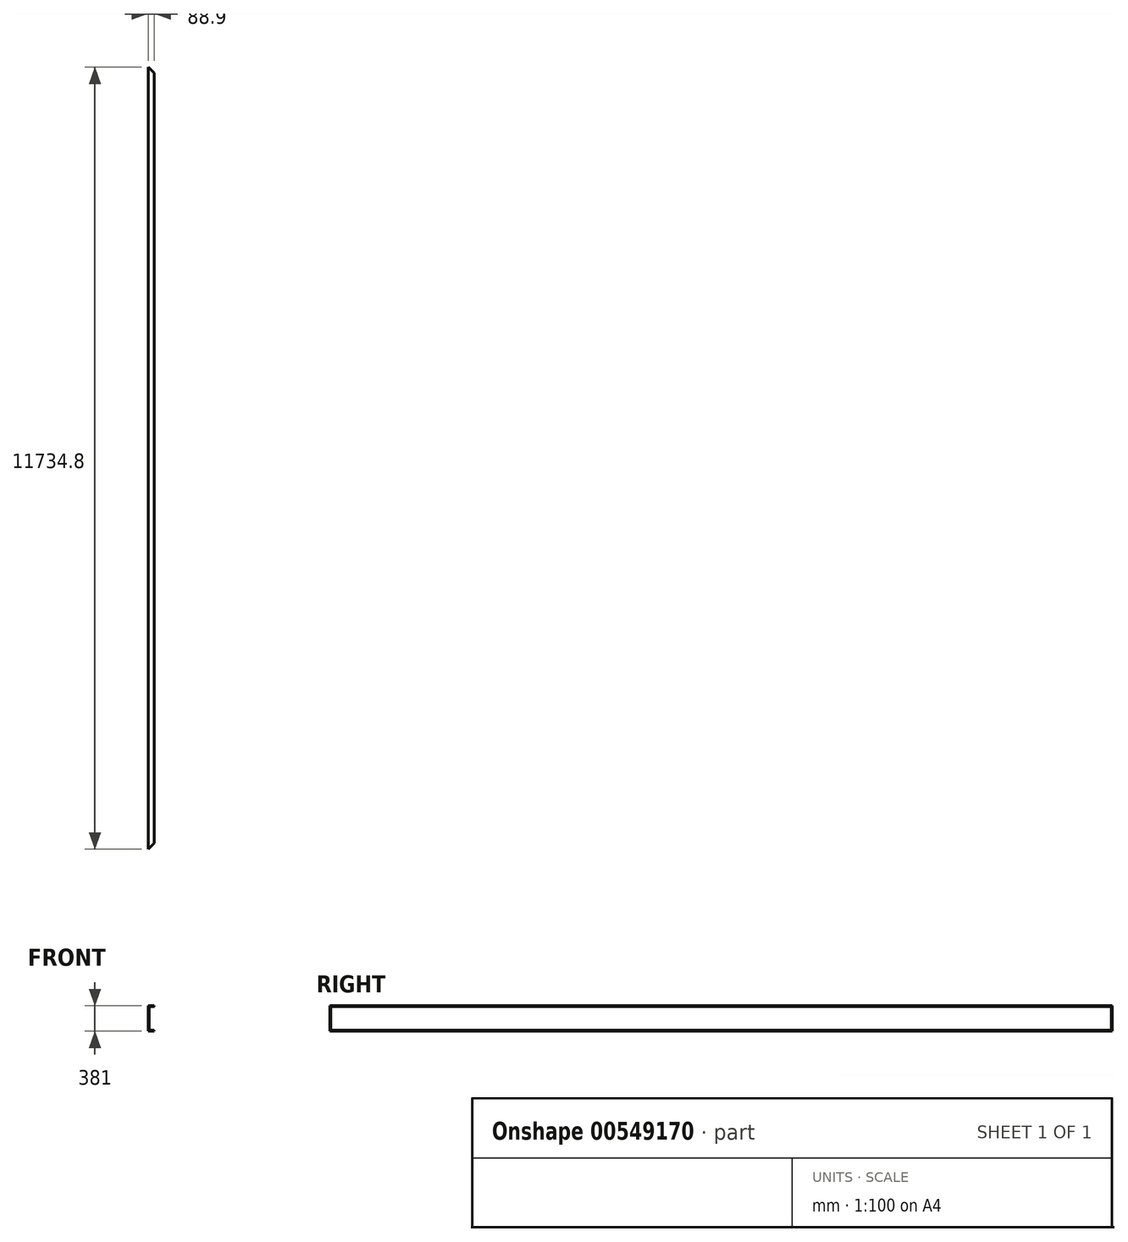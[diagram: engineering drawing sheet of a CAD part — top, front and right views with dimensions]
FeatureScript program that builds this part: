
annotation { "Feature Type Name" : "Feature", "Feature Type Description" : "" }
export const myFeature = defineFeature(function(context is Context, id is Id, definition is map)
    precondition{}
    {
        {
            var Q0;
            Q0=qCreatedBy(makeId("Front.planeOp"),FACE);
            var sketch = newSketch(context, id + "F0", { "sketchPlane" : qUnion([Q0])});
            skLineSegment(sketch, "E0", {"start": v(44.45, 190.5) * mm, "end": v(-44.45, 190.5) * mm});
            skLineSegment(sketch, "E1", {"start": v(-44.45, 190.5) * mm, "end": v(-44.45, -190.5) * mm});
            skLineSegment(sketch, "E2", {"start": v(-44.45, -190.5) * mm, "end": v(44.45, -190.5) * mm});
            skLineSegment(sketch, "E3", {"start": v(44.45, -190.5) * mm, "end": v(44.45, -177.8) * mm});
            skLineSegment(sketch, "E4", {"start": v(44.45, -177.8) * mm, "end": v(-31.75, -177.8) * mm});
            skLineSegment(sketch, "E5", {"start": v(-31.75, -177.8) * mm, "end": v(-31.75, 177.8) * mm});
            skLineSegment(sketch, "E6", {"start": v(-31.75, 177.8) * mm, "end": v(44.45, 177.8) * mm});
            skLineSegment(sketch, "E7", {"start": v(44.45, 177.8) * mm, "end": v(44.45, 190.5) * mm});
            skSolve(sketch);
        }
        {
            var Q0;
            Q0=makeQuery(id+"F0.imprint","IMPRINT",FACE,{"disambiguationData":[TD([[makeQuery(id+"F0.imprint","IMPRINT",EDGE,{"derivedFrom":sQuery(id+"F0.wireOp",EDGE,"E0")}),1.0]])]});
            extrude(context, id + "F1", {"entities" : qUnion([Q0]), "depth" : 11734.8 * mm});
        }
        {
            var Q0;
            Q0=makeQuery(id+"F1.opExtrude","SWEPT_EDGE",EDGE,{"disambiguationData":[OSD([sQuery(id+"F0.wireOp",EDGE,"E3"),sQuery(id+"F0.wireOp",EDGE,"E4")])]});
            var Q1;
            Q1=makeQuery(id+"F1.opExtrude","SWEPT_EDGE",EDGE,{"disambiguationData":[OSD([sQuery(id+"F0.wireOp",EDGE,"E4"),sQuery(id+"F0.wireOp",EDGE,"E5")])]});
            var Q2;
            Q2=makeQuery(id+"F1.opExtrude","SWEPT_EDGE",EDGE,{"disambiguationData":[OSD([sQuery(id+"F0.wireOp",EDGE,"E5"),sQuery(id+"F0.wireOp",EDGE,"E6")])]});
            var Q3;
            Q3=makeQuery(id+"F1.opExtrude","SWEPT_EDGE",EDGE,{"disambiguationData":[OSD([sQuery(id+"F0.wireOp",EDGE,"E6"),sQuery(id+"F0.wireOp",EDGE,"E7")])]});
            fillet(context, id + "F2", {"entities" : qUnion([Q0, Q1, Q2, Q3]), "radius" : 7.62 * mm, "tangentPropagation" : true, "allowEdgeOverflow" : false});
        }
        {
            var Q0;
            Q0=makeQuery(id+"F1.opExtrude","SWEPT_FACE",FACE,{"disambiguationData":[OSD([sQuery(id+"F0.wireOp",EDGE,"E0")])]});
            var sketch = newSketch(context, id + "F3", { "sketchPlane" : qUnion([Q0])});
            skLineSegment(sketch, "E8", {"start": v(-44.45, 0) * mm, "end": v(44.45, -88.9) * mm});
            skLineSegment(sketch, "E9", {"start": v(-44.45, -11734.8) * mm, "end": v(44.45, -11645.9) * mm});
            skSolve(sketch);
        }
        {
            var Q0;
            {var subQ0=sQuery(id+"F3.wireOp",EDGE,"E8");Q0=makeQuery(id+"F3.imprint","IMPRINT",FACE,{"disambiguationData":[TD([[makeQuery(id+"F3.imprint","IMPRINT",EDGE,{"derivedFrom":subQ0}),1.0]])]});}
            extrude(context, id + "F4", {"entities" : qUnion([Q0]), "operationType" : NewBodyOperationType.REMOVE, "endBound" : BoundingType.THROUGH_ALL, "oppositeDirection" : true, "depth" : 25.4 * mm});
        }
        {
            var Q0;
            {var subQ0=sQuery(id+"F3.wireOp",EDGE,"E9");Q0=makeQuery(id+"F3.imprint","IMPRINT",FACE,{"disambiguationData":[TD([[makeQuery(id+"F3.imprint","IMPRINT",EDGE,{"derivedFrom":subQ0}),-1.0]])]});}
            extrude(context, id + "F5", {"entities" : qUnion([Q0]), "operationType" : NewBodyOperationType.REMOVE, "endBound" : BoundingType.THROUGH_ALL, "oppositeDirection" : true, "depth" : 25.4 * mm});
        }
    });
